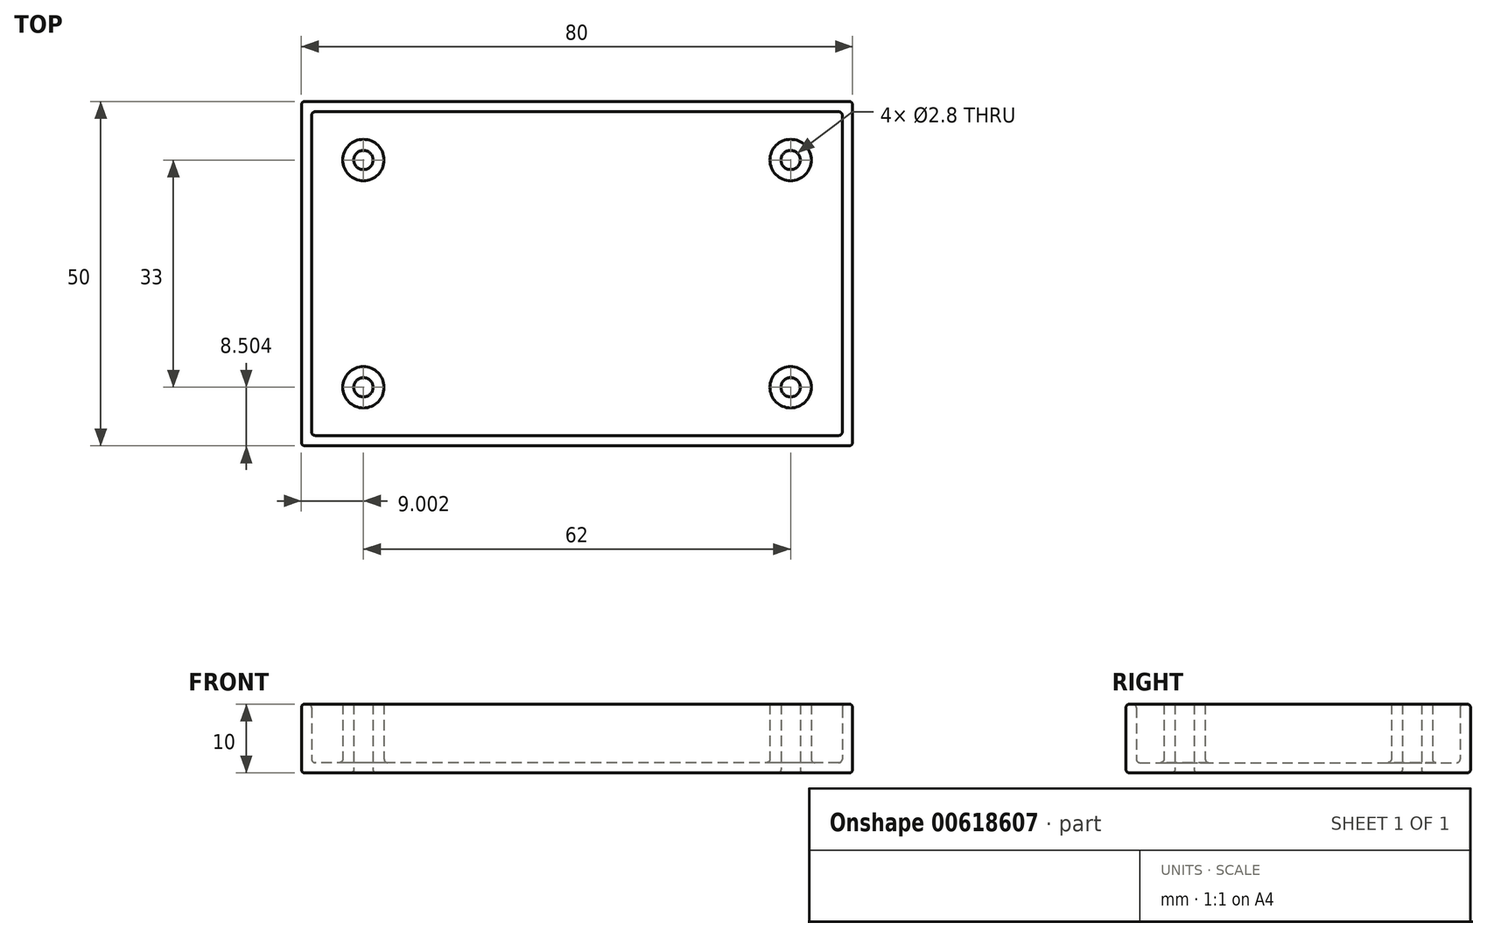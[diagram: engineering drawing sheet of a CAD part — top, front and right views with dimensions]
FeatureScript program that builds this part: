
annotation { "Feature Type Name" : "Feature", "Feature Type Description" : "" }
export const myFeature = defineFeature(function(context is Context, id is Id, definition is map)
    precondition{}
    {
        {
            var Q0;
            Q0=qCreatedBy(makeId("Top.planeOp"),FACE);
            var sketch = newSketch(context, id + "F0", { "sketchPlane" : qUnion([Q0])});
            skLineSegment(sketch, "E0.bottom", {"start": v(-52.19, 52.66) * mm, "end": v(27.81, 52.66) * mm});
            skLineSegment(sketch, "E0.top", {"start": v(-52.19, 2.66) * mm, "end": v(27.81, 2.66) * mm});
            skLineSegment(sketch, "E0.left", {"start": v(-52.19, 52.66) * mm, "end": v(-52.19, 2.66) * mm});
            skLineSegment(sketch, "E0.right", {"start": v(27.81, 52.66) * mm, "end": v(27.81, 2.66) * mm});
            skPoint(sketch, "E1", {"position": v(-43.19, 44.16) * mm});
            skPoint(sketch, "E2", {"position": v(-43.19, 11.16) * mm});
            skPoint(sketch, "E3", {"position": v(18.81, 11.16) * mm});
            skPoint(sketch, "E4", {"position": v(18.81, 44.16) * mm});
            skCircle(sketch, "E5", {"center": v(-43.19, 44.16) * mm, "radius": 3 * mm});
            skCircle(sketch, "E6", {"center": v(-43.19, 11.16) * mm, "radius": 3 * mm});
            skCircle(sketch, "E7", {"center": v(18.81, 11.16) * mm, "radius": 3 * mm});
            skCircle(sketch, "E8", {"center": v(18.81, 44.16) * mm, "radius": 3 * mm});
            skLineSegment(sketch, "E9.bottom", {"start": v(-50.69, 51.16) * mm, "end": v(26.31, 51.16) * mm});
            skLineSegment(sketch, "E9.top", {"start": v(-50.69, 4.16) * mm, "end": v(26.31, 4.16) * mm});
            skLineSegment(sketch, "E9.left", {"start": v(-50.69, 51.16) * mm, "end": v(-50.69, 4.16) * mm});
            skLineSegment(sketch, "E9.right", {"start": v(26.31, 51.16) * mm, "end": v(26.31, 4.16) * mm});
            skSolve(sketch);
        }
        {
            var Q0;
            Q0 = qSketchRegion(id + "F0", true);
            var Q1;
            Q1=makeQuery(id+"F0.imprint","IMPRINT",FACE,{"disambiguationData":[TD([[makeQuery(id+"F0.imprint","IMPRINT",EDGE,{"derivedFrom":sQuery(id+"F0.wireOp",EDGE,"E5")}),-1.0]])]});
            var Q2;
            Q2=makeQuery(id+"F0.imprint","IMPRINT",FACE,{"disambiguationData":[TD([[makeQuery(id+"F0.imprint","IMPRINT",EDGE,{"derivedFrom":sQuery(id+"F0.wireOp",EDGE,"E7")}),1.0]])]});
            var Q3;
            Q3=makeQuery(id+"F0.imprint","IMPRINT",FACE,{"disambiguationData":[TD([[makeQuery(id+"F0.imprint","IMPRINT",EDGE,{"derivedFrom":sQuery(id+"F0.wireOp",EDGE,"E6")}),1.0]])]});
            var Q4;
            Q4=makeQuery(id+"F0.imprint","IMPRINT",FACE,{"disambiguationData":[TD([[makeQuery(id+"F0.imprint","IMPRINT",EDGE,{"derivedFrom":sQuery(id+"F0.wireOp",EDGE,"E5")}),1.0]])]});
            var Q5;
            Q5=makeQuery(id+"F0.imprint","IMPRINT",FACE,{"disambiguationData":[TD([[makeQuery(id+"F0.imprint","IMPRINT",EDGE,{"derivedFrom":sQuery(id+"F0.wireOp",EDGE,"E8")}),1.0]])]});
            extrude(context, id + "F1", {"entities" : qUnion([Q0, Q1, Q2, Q3, Q4, Q5]), "depth" : 1.5 * mm, "offsetDistance" : 25 * mm});
        }
        {
            var Q0;
            Q0=makeQuery(id+"F0.imprint","IMPRINT",FACE,{"disambiguationData":[TD([[makeQuery(id+"F0.imprint","IMPRINT",EDGE,{"derivedFrom":sQuery(id+"F0.wireOp",EDGE,"E7")}),1.0]])]});
            var Q1;
            Q1=makeQuery(id+"F0.imprint","IMPRINT",FACE,{"disambiguationData":[TD([[makeQuery(id+"F0.imprint","IMPRINT",EDGE,{"derivedFrom":sQuery(id+"F0.wireOp",EDGE,"E8")}),1.0]])]});
            var Q2;
            Q2=makeQuery(id+"F0.imprint","IMPRINT",FACE,{"disambiguationData":[TD([[makeQuery(id+"F0.imprint","IMPRINT",EDGE,{"derivedFrom":sQuery(id+"F0.wireOp",EDGE,"E5")}),1.0]])]});
            var Q3;
            Q3=makeQuery(id+"F0.imprint","IMPRINT",FACE,{"disambiguationData":[TD([[makeQuery(id+"F0.imprint","IMPRINT",EDGE,{"derivedFrom":sQuery(id+"F0.wireOp",EDGE,"E6")}),1.0]])]});
            var Q4;
            Q4=makeQuery(id+"F0.imprint","IMPRINT",FACE,{"disambiguationData":[TD([[makeQuery(id+"F0.imprint","IMPRINT",EDGE,{"derivedFrom":sQuery(id+"F0.wireOp",EDGE,"E0.bottom")}),-1.0]])]});
            extrude(context, id + "F2", {"entities" : qUnion([Q0, Q1, Q2, Q3, Q4]), "operationType" : NewBodyOperationType.ADD, "depth" : 10 * mm, "offsetDistance" : 25 * mm});
        }
        {
            var Q0;
            Q0=sQuery(id+"F0.wireOp",VERTEX,"E3");
            var Q1;
            Q1=sQuery(id+"F0.wireOp",VERTEX,"E2");
            var Q2;
            Q2=sQuery(id+"F0.wireOp",VERTEX,"E1");
            var Q3;
            Q3=sQuery(id+"F0.wireOp",VERTEX,"E4");
            var Q4;
            Q4=makeQuery(id+"F1.opExtrude","SWEPT_BODY",BODY,{"disambiguationData":[OSD([sQuery(id+"F0.wireOp",EDGE,"E0.bottom"),sQuery(id+"F0.wireOp",EDGE,"E0.top"),sQuery(id+"F0.wireOp",EDGE,"E0.left"),sQuery(id+"F0.wireOp",EDGE,"E0.right")])]});
            hole(context, id + "F3", {"style" : HoleStyle.SIMPLE, "endStyle" : HoleEndStyle.THROUGH, "oppositeDirection" : true, "holeDiameter" : 2.8 * mm, "majorDiameter" : 5 * mm, "isTappedThrough" : true, "tappedDepth" : 12 * mm, "tapClearance" : 3, "locations" : qUnion([Q0, Q1, Q2, Q3]), "scope" : qUnion([Q4])});
        }
        {
            var Q0;
            Q0=makeQuery(id+"F1.opExtrude","CAP_FACE",FACE,{"disambiguationData":[OSD([sQuery(id+"F0.wireOp",EDGE,"E0.bottom"),sQuery(id+"F0.wireOp",EDGE,"E0.top"),sQuery(id+"F0.wireOp",EDGE,"E0.left"),sQuery(id+"F0.wireOp",EDGE,"E0.right")])],"isStart":false});
            var Q1;
            Q1=makeQuery(id+"F1.opExtrude","CAP_FACE",FACE,{"disambiguationData":[OSD([sQuery(id+"F0.wireOp",EDGE,"E0.bottom"),sQuery(id+"F0.wireOp",EDGE,"E0.top"),sQuery(id+"F0.wireOp",EDGE,"E0.left"),sQuery(id+"F0.wireOp",EDGE,"E0.right")])],"isStart":true});
            var Q2;
            {var subQ0=sQuery(id+"F0.wireOp",EDGE,"E0.left");var subQ1=sQuery(id+"F0.wireOp",EDGE,"E0.top");Q2=makeQuery(id+"F2.boolean.opBoolean","MERGE",EDGE,{"derivedFrom":[makeQuery(id+"F1.opExtrude","SWEPT_EDGE",EDGE,{"disambiguationData":[OSD([subQ1,subQ0])]}),makeQuery(id+"F2.opExtrude","SWEPT_EDGE",EDGE,{"disambiguationData":[OSD([subQ1,subQ0])]})]});}
            var Q3;
            Q3=makeQuery(id+"F2.opExtrude","CAP_EDGE",EDGE,{"disambiguationData":[OSD([sQuery(id+"F0.wireOp",EDGE,"E0.top")])],"isStart":false});
            var Q4;
            {var subQ0=sQuery(id+"F0.wireOp",EDGE,"E0.left");Q4=makeQuery(id+"F2.boolean.opBoolean","MERGE",FACE,{"derivedFrom":[makeQuery(id+"F1.opExtrude","SWEPT_FACE",FACE,{"disambiguationData":[OSD([subQ0])]}),makeQuery(id+"F2.opExtrude","SWEPT_FACE",FACE,{"disambiguationData":[OSD([subQ0])]})]});}
            var Q5;
            {var subQ0=sQuery(id+"F0.wireOp",EDGE,"E0.top");Q5=makeQuery(id+"F2.boolean.opBoolean","MERGE",FACE,{"derivedFrom":[makeQuery(id+"F1.opExtrude","SWEPT_FACE",FACE,{"disambiguationData":[OSD([subQ0])]}),makeQuery(id+"F2.opExtrude","SWEPT_FACE",FACE,{"disambiguationData":[OSD([subQ0])]})]});}
            var Q6;
            {var subQ0=sQuery(id+"F0.wireOp",EDGE,"E0.right");Q6=makeQuery(id+"F2.boolean.opBoolean","MERGE",FACE,{"derivedFrom":[makeQuery(id+"F1.opExtrude","SWEPT_FACE",FACE,{"disambiguationData":[OSD([subQ0])]}),makeQuery(id+"F2.opExtrude","SWEPT_FACE",FACE,{"disambiguationData":[OSD([subQ0])]})]});}
            var Q7;
            {var subQ0=sQuery(id+"F0.wireOp",EDGE,"E0.bottom");Q7=makeQuery(id+"F2.boolean.opBoolean","MERGE",FACE,{"derivedFrom":[makeQuery(id+"F1.opExtrude","SWEPT_FACE",FACE,{"disambiguationData":[OSD([subQ0])]}),makeQuery(id+"F2.opExtrude","SWEPT_FACE",FACE,{"disambiguationData":[OSD([subQ0])]})]});}
            var Q8;
            Q8=makeQuery(id+"F2.opExtrude","SWEPT_FACE",FACE,{"disambiguationData":[OSD([sQuery(id+"F0.wireOp",EDGE,"E9.right")])]});
            var Q9;
            Q9=makeQuery(id+"F2.opExtrude","SWEPT_FACE",FACE,{"disambiguationData":[OSD([sQuery(id+"F0.wireOp",EDGE,"E9.bottom")])]});
            var Q10;
            Q10=makeQuery(id+"F2.opExtrude","SWEPT_FACE",FACE,{"disambiguationData":[OSD([sQuery(id+"F0.wireOp",EDGE,"E9.left")])]});
            var Q11;
            Q11=makeQuery(id+"F2.opExtrude","SWEPT_FACE",FACE,{"disambiguationData":[OSD([sQuery(id+"F0.wireOp",EDGE,"E9.top")])]});
            fillet(context, id + "F4", {"entities" : qUnion([Q0, Q1, Q2, Q3, Q4, Q5, Q6, Q7, Q8, Q9, Q10, Q11]), "radius" : .5 * mm, "tangentPropagation" : true, "allowEdgeOverflow" : false});
        }
    });
